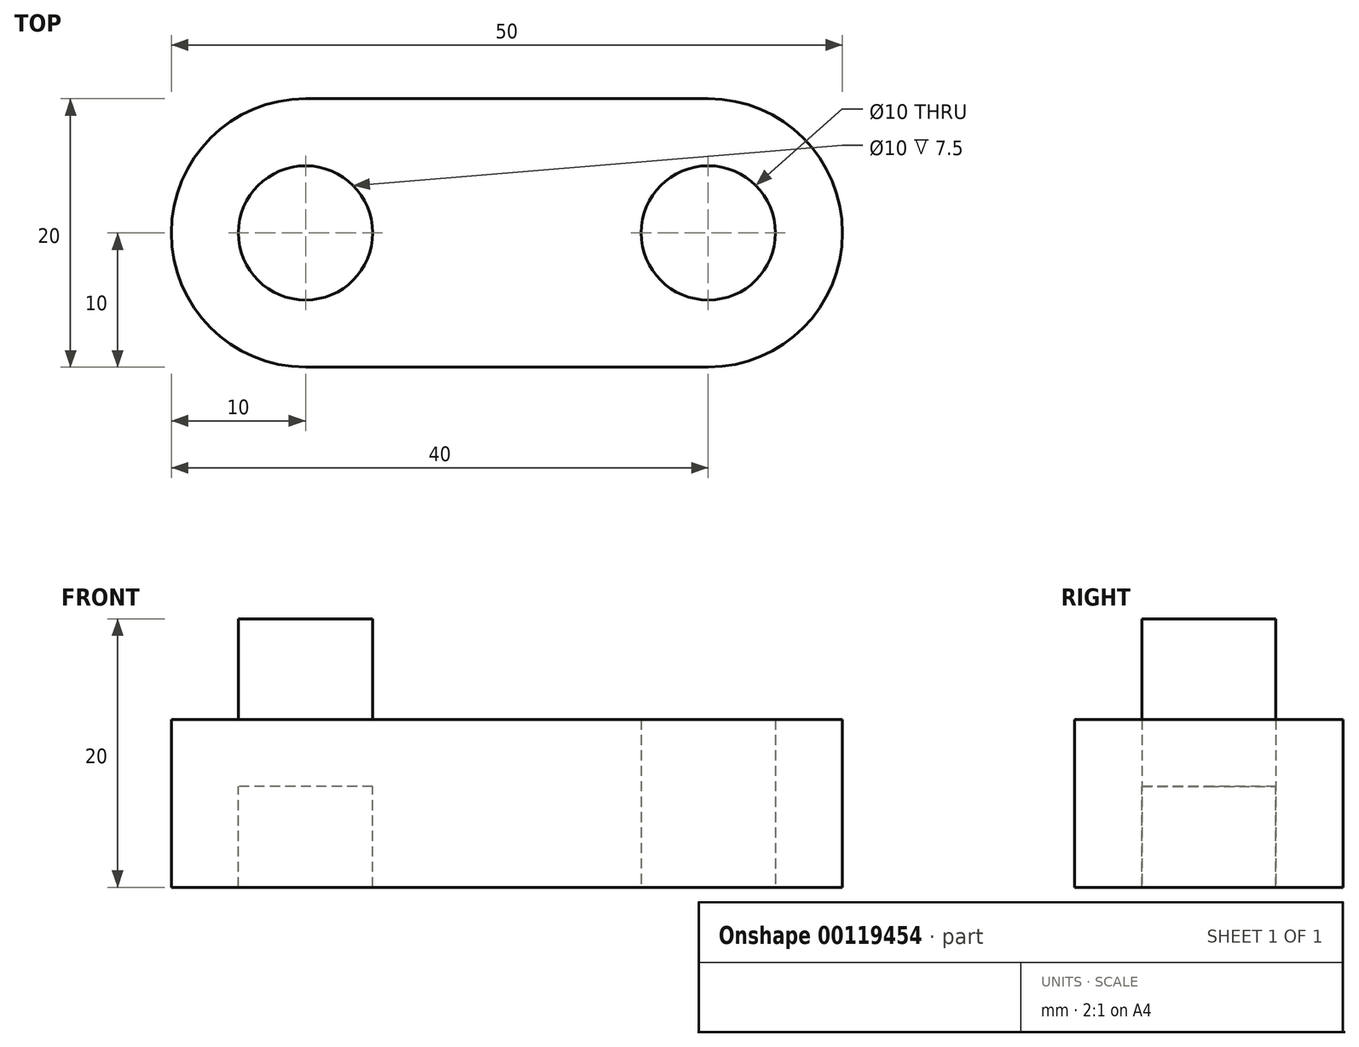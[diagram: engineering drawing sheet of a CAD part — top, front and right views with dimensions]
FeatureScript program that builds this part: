
annotation { "Feature Type Name" : "Feature", "Feature Type Description" : "" }
export const myFeature = defineFeature(function(context is Context, id is Id, definition is map)
    precondition{}
    {
        {
            var Q0;
            Q0=qCreatedBy(makeId("Top.planeOp"),FACE);
            var sketch = newSketch(context, id + "F0", { "sketchPlane" : qUnion([Q0])});
            skLineSegment(sketch, "E0.bottom", {"start": v(15, -10) * mm, "end": v(-15, -10) * mm});
            skLineSegment(sketch, "E0.top", {"start": v(15, 10) * mm, "end": v(-15, 10) * mm});
            skPoint(sketch, "E0.middle", {"position": v(0, 0) * mm});
            skCircle(sketch, "E1", {"center": v(-15, 0) * mm, "radius": 5 * mm});
            skLineSegment(sketch, "E2", {"start": v(0, 19.17) * mm, "end": v(0, -24.1) * mm, "construction": true});
            skCircle(sketch, "E3.MirrorC", {"center": v(15, 0) * mm, "radius": 5 * mm});
            skArc(sketch, "E4", {"start": v(-15, 10) * mm, "mid": v(-25, 0) * mm, "end": v(-15, -10) * mm});
            skArc(sketch, "E5", {"start": v(15, 10) * mm, "mid": v(25, 0) * mm, "end": v(15, -10) * mm});
            skSolve(sketch);
        }
        {
            var Q0;
            Q0=makeQuery(id+"F0.imprint","IMPRINT",FACE,{"disambiguationData":[TD([[makeQuery(id+"F0.imprint","IMPRINT",EDGE,{"derivedFrom":sQuery(id+"F0.wireOp",EDGE,"E0.bottom")}),-1.0]])]});
            var Q1;
            Q1=makeQuery(id+"F0.imprint","IMPRINT",FACE,{"disambiguationData":[TD([[makeQuery(id+"F0.imprint","IMPRINT",EDGE,{"derivedFrom":sQuery(id+"F0.wireOp",EDGE,"E1")}),1.0]])]});
            var Q2;
            Q2=makeQuery(id+"F0.imprint","IMPRINT",FACE,{"disambiguationData":[TD([[makeQuery(id+"F0.imprint","IMPRINT",EDGE,{"derivedFrom":sQuery(id+"F0.wireOp",EDGE,"E3.MirrorC")}),-1.0]])]});
            extrude(context, id + "F1", {"entities" : qUnion([Q0, Q1, Q2]), "endBound" : BoundingType.SYMMETRIC, "depth" : 5 * mm});
        }
        {
            var Q0;
            Q0=makeQuery(id+"F0.imprint","IMPRINT",FACE,{"disambiguationData":[TD([[makeQuery(id+"F0.imprint","IMPRINT",EDGE,{"derivedFrom":sQuery(id+"F0.wireOp",EDGE,"E1")}),1.0]])]});
            extrude(context, id + "F2", {"entities" : qUnion([Q0]), "operationType" : NewBodyOperationType.ADD, "depth" : 10 * mm});
        }
        {
            var Q0;
            Q0=makeQuery(id+"F0.imprint","IMPRINT",FACE,{"disambiguationData":[TD([[makeQuery(id+"F0.imprint","IMPRINT",EDGE,{"derivedFrom":sQuery(id+"F0.wireOp",EDGE,"E3.MirrorC")}),-1.0]])]});
            extrude(context, id + "F3", {"entities" : qUnion([Q0]), "operationType" : NewBodyOperationType.ADD, "oppositeDirection" : true, "depth" : 10 * mm});
        }
    });
